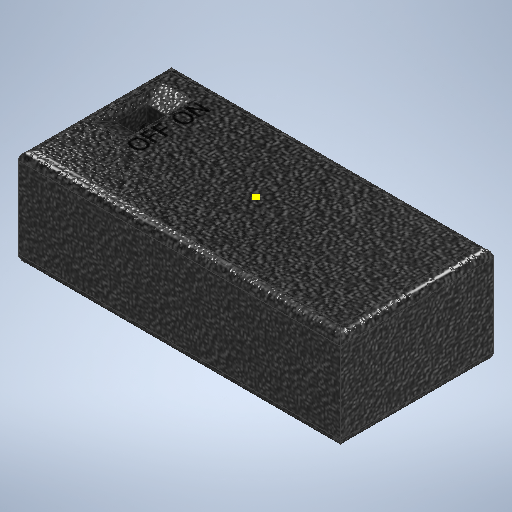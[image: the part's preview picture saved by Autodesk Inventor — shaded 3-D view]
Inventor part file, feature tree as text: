
AUTODESK INVENTOR PART (.ipt)
format: ipt  version: 2025.2 (Build 292293000, 293)  size: 396,288 bytes
history: native  units: in
note: dims shown in document units (in); Inventor stores cm internally (conversion verified against a paired STEP export)
features: draft x4, sketch x4, extrude x3, fillet x1
ambient origin geometry x8: Origin, YZ Plane, XZ Plane, XY Plane, X Axis, Y Axis, Z Axis, Center Point
bodies: Solid1 (feature_tree)
feature tree (12):
  extrude  "Extrusion1"  Depth=1.25in
  fillet  "Fillet1"  Radius=0.625in
  extrude  "Extrusion2"  Depth=0.8125in TaperAngle=0.0deg
  extrude  "Extrusion3"  Depth=0.25in
  draft  "FaceDraft1"
  draft  "FaceDraft2"
  draft  "FaceDraft3"
  draft  "FaceDraft4"
  sketch  "Sketch4"  dims[d8=0.5625in d9=0.1875in d10=0.25in d11=0.1565in d12=0.031in d13=0.1875in d14=0.0in d15=0.25in d16=0.5625in d17=0.1565in d19=0.0312in d20=0.0625in d21=0.0in d22=0.1855in d23=0.1855in d24=0.1512in d25=0.1512in]
  sketch  "Sketch1"  dims[d0=2.625in d1=1.25in d2=0.625in]
  sketch  "Sketch2"  dims[d3=1.3125in d4=0.8125in d5=0.0in]
  sketch  "Sketch3"  dims[d6=0.075in d7=0.25in]
